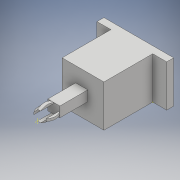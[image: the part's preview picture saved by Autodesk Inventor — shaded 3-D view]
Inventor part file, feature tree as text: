
AUTODESK INVENTOR PART (.ipt)
format: ipt  version: 2018 (Build 220112000, 112)  size: 172,544 bytes
history: native  units: mm
features: sketch x12, extrude x7
ambient origin geometry x8: Origin, YZ Plane, XZ Plane, XY Plane, X Axis, Y Axis, Z Axis, Center Point
bodies: Solid1 (feature_tree)
feature tree (19):
  extrude  "Extrusion1"  Depth=10.0mm
  sketch  "Sketch2"  dims[d2=60.0mm d3=70.0mm]
  extrude  "Extrusion2"  Depth=70.0mm
  extrude  "Extrusion3"  Depth=40.0mm TaperAngle=0.0deg
  sketch  "Sketch5"  dims[d13=20.0mm d14=0.0mm d15=20.0mm d16=0.0mm]
  sketch  "Sketch6"  dims[d17=20.0mm d18=0.0mm]
  sketch  "Sketch7"
  sketch  "Sketch8"
  extrude  "Extrusion4"  Depth=20.0mm TaperAngle=0.0deg
  extrude  "Extrusion5"  Depth=20.0mm TaperAngle=0.0deg
  extrude  "Extrusion6"  [1 undecoded]
  extrude  "Extrusion7"  [1 undecoded]
  sketch  "Sketch1"  dims[d0=100.0mm d1=10.0mm]
  sketch  "Sketch3"  dims[d4=60.0mm d5=0.0mm d6=40.0mm d7=0.0mm]
  sketch  "Sketch4"  dims[d8=20.0mm d9=0.0mm d11=20.0mm d12=0.0mm]
  sketch  "Sketch9"
  sketch  "Sketch10"
  sketch  "Sketch11"
  sketch  "Sketch12"
note: 2 required parameter values undecoded (feature->parameter linkage not recoverable at this tier; creation-order binding heuristic only, values carry confidence <= 0.55)
